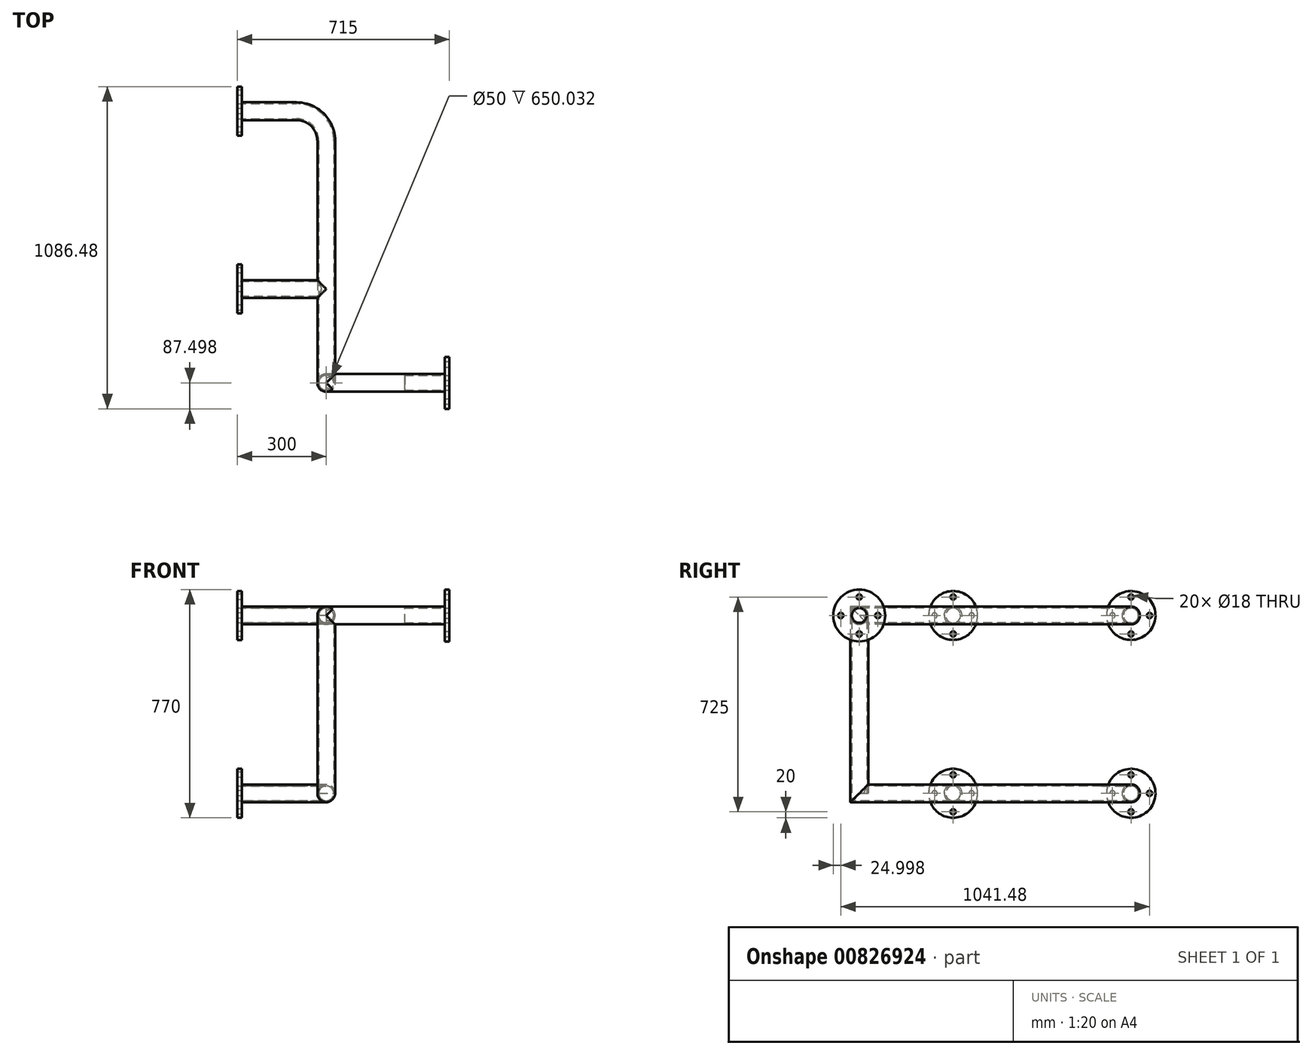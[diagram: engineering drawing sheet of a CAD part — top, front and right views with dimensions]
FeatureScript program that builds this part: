
annotation { "Feature Type Name" : "Feature", "Feature Type Description" : "" }
export const myFeature = defineFeature(function(context is Context, id is Id, definition is map)
    precondition{}
    {
        {
            var Q0;
            Q0=qCreatedBy(makeId("Top.planeOp"),FACE);
            var sketch = newSketch(context, id + "F0", { "sketchPlane" : qUnion([Q0])});
            skLineSegment(sketch, "E0.bottom", {"start": v(0, 0) * mm, "end": v(200, 0) * mm});
            skLineSegment(sketch, "E0.top", {"start": v(0, -600) * mm, "end": v(300, -600) * mm});
            skLineSegment(sketch, "E0.right", {"start": v(300, -100) * mm, "end": v(300, -600) * mm});
            skLineSegment(sketch, "E1", {"start": v(300, -600) * mm, "end": v(300, -916.48) * mm});
            skPoint(sketch, "E2.visualSharp", {"position": v(300, 0) * mm});
            skArc(sketch, "E2.filletArc", {"start": v(300, -100) * mm, "mid": v(270.71, -29.29) * mm, "end": v(200, 0) * mm});
            skSolve(sketch);
        }
        {
            var Q0;
            Q0=qCreatedBy(makeId("Top.planeOp"),FACE);
            cPlane(context, id + "F1", {"entities" : qUnion([Q0]), "cplaneType" : CPlaneType.OFFSET, "offset" : 600 * mm, "width" : 150 * mm, "height" : 150 * mm});
        }
        {
            var Q0;
            Q0=qCreatedBy(makeId("Right.planeOp"),FACE);
            cPlane(context, id + "F2", {"entities" : qUnion([Q0]), "cplaneType" : CPlaneType.OFFSET, "offset" : 300 * mm, "width" : 150 * mm, "height" : 150 * mm});
        }
        {
            var Q0;
            Q0=qCreatedBy(id+"F1.planeOp",FACE);
            var sketch = newSketch(context, id + "F3", { "sketchPlane" : qUnion([Q0])});
            skLineSegment(sketch, "E3.0", {"start": v(0, 0) * mm, "end": v(200, 0) * mm});
            skLineSegment(sketch, "E3.1", {"start": v(300, -100) * mm, "end": v(300, -600) * mm});
            skLineSegment(sketch, "E3.2", {"start": v(0, -600) * mm, "end": v(300, -600) * mm});
            skLineSegment(sketch, "E3.3", {"start": v(300, -600) * mm, "end": v(300, -916.48) * mm});
            skArc(sketch, "E3.4", {"start": v(300, -100) * mm, "mid": v(270.71, -29.29) * mm, "end": v(200, 0) * mm});
            skSolve(sketch);
        }
        {
            var Q0;
            Q0=qCreatedBy(makeId("Right.planeOp"),FACE);
            var sketch = newSketch(context, id + "F4", { "sketchPlane" : qUnion([Q0])});
            skCircle(sketch, "E4", {"center": v(0, 0) * mm, "radius": 25 * mm});
            skCircle(sketch, "E5", {"center": v(0, 0) * mm, "radius": 30 * mm});
            skCircle(sketch, "E6.0.1.0", {"center": v(0, 600) * mm, "radius": 30 * mm});
            skCircle(sketch, "E6.0.1.1", {"center": v(0, 600) * mm, "radius": 25 * mm});
            skCircle(sketch, "E6.1.0.0", {"center": v(-600, 0) * mm, "radius": 30 * mm});
            skCircle(sketch, "E6.1.0.1", {"center": v(-600, 0) * mm, "radius": 25 * mm});
            skCircle(sketch, "E6.1.1.0", {"center": v(-600, 600) * mm, "radius": 30 * mm});
            skCircle(sketch, "E6.1.1.1", {"center": v(-600, 600) * mm, "radius": 25 * mm});
            skLineSegment(sketch, "E6.direction1", {"start": v(0, 0) * mm, "end": v(-600, 0) * mm, "construction": true});
            skLineSegment(sketch, "E6.direction2", {"start": v(0, 0) * mm, "end": v(0, 600) * mm, "construction": true});
            skSolve(sketch);
        }
        {
            var Q0;
            Q0=makeQuery(id+"F4.imprint","IMPRINT",FACE,{"disambiguationData":[TD([[makeQuery(id+"F4.imprint","IMPRINT",EDGE,{"derivedFrom":sQuery(id+"F4.wireOp",EDGE,"E6.0.1.0")}),1.0]])]});
            var sketch = newSketch(context, id + "F5", { "sketchPlane" : qUnion([Q0])});
            skPoint(sketch, "E7.0", {"position": v(0, 600) * mm});
            skCircle(sketch, "E8", {"center": v(0, 600) * mm, "radius": 82.5 * mm});
            skCircle(sketch, "E9", {"center": v(0, 662.5) * mm, "radius": 9 * mm});
            skCircle(sketch, "E10.1.0", {"center": v(-62.5, 600) * mm, "radius": 9 * mm});
            skCircle(sketch, "E10.2.0", {"center": v(0, 537.5) * mm, "radius": 9 * mm});
            skCircle(sketch, "E10.3.0", {"center": v(62.5, 600) * mm, "radius": 9 * mm});
            skCircle(sketch, "E11.0.0", {"center": v(0, 600) * mm, "radius": 25 * mm});
            skCircle(sketch, "E12.0.1.0", {"center": v(0, -62.5) * mm, "radius": 9 * mm});
            skCircle(sketch, "E12.0.1.1", {"center": v(-62.5, 0) * mm, "radius": 9 * mm});
            skCircle(sketch, "E12.0.1.2", {"center": v(0, 0) * mm, "radius": 82.5 * mm});
            skCircle(sketch, "E12.0.1.3", {"center": v(62.5, 0) * mm, "radius": 9 * mm});
            skPoint(sketch, "E12.0.1.4", {"position": v(0, 0) * mm});
            skCircle(sketch, "E12.0.1.5", {"center": v(0, 62.5) * mm, "radius": 9 * mm});
            skCircle(sketch, "E12.0.1.6", {"center": v(0, 0) * mm, "radius": 25 * mm});
            skPoint(sketch, "E12.0.1.7", {"position": v(0, 0) * mm});
            skCircle(sketch, "E12.1.0.0", {"center": v(-600, 537.5) * mm, "radius": 9 * mm});
            skCircle(sketch, "E12.1.0.1", {"center": v(-662.5, 600) * mm, "radius": 9 * mm});
            skCircle(sketch, "E12.1.0.2", {"center": v(-600, 600) * mm, "radius": 82.5 * mm});
            skCircle(sketch, "E12.1.0.3", {"center": v(-537.5, 600) * mm, "radius": 9 * mm});
            skPoint(sketch, "E12.1.0.4", {"position": v(-600, 600) * mm});
            skCircle(sketch, "E12.1.0.5", {"center": v(-600, 662.5) * mm, "radius": 9 * mm});
            skCircle(sketch, "E12.1.0.6", {"center": v(-600, 600) * mm, "radius": 25 * mm});
            skPoint(sketch, "E12.1.0.7", {"position": v(-600, 600) * mm});
            skCircle(sketch, "E12.1.1.0", {"center": v(-600, -62.5) * mm, "radius": 9 * mm});
            skCircle(sketch, "E12.1.1.1", {"center": v(-662.5, 0) * mm, "radius": 9 * mm});
            skCircle(sketch, "E12.1.1.2", {"center": v(-600, 0) * mm, "radius": 82.5 * mm});
            skCircle(sketch, "E12.1.1.3", {"center": v(-537.5, 0) * mm, "radius": 9 * mm});
            skPoint(sketch, "E12.1.1.4", {"position": v(-600, 0) * mm});
            skCircle(sketch, "E12.1.1.5", {"center": v(-600, 62.5) * mm, "radius": 9 * mm});
            skCircle(sketch, "E12.1.1.6", {"center": v(-600, 0) * mm, "radius": 25 * mm});
            skPoint(sketch, "E12.1.1.7", {"position": v(-600, 0) * mm});
            skLineSegment(sketch, "E12.direction1", {"start": v(0, 537.5) * mm, "end": v(-600, 537.5) * mm, "construction": true});
            skLineSegment(sketch, "E12.direction2", {"start": v(0, 537.5) * mm, "end": v(0, -62.5) * mm, "construction": true});
            skSolve(sketch);
        }
        {
            var Q0;
            Q0=qCreatedBy(id+"F2.planeOp",FACE);
            var sketch = newSketch(context, id + "F6", { "sketchPlane" : qUnion([Q0])});
            skLineSegment(sketch, "E13.0", {"start": v(-600, 600) * mm, "end": v(-916.48, 600) * mm});
            skLineSegment(sketch, "E14.0", {"start": v(-600, 0) * mm, "end": v(-916.48, 0) * mm});
            skLineSegment(sketch, "E15", {"start": v(-916.48, 600) * mm, "end": v(-916.48, 0) * mm});
            skSolve(sketch);
        }
        {
            var Q0;
            Q0=makeQuery(id+"F4.imprint","IMPRINT",FACE,{"disambiguationData":[TD([[makeQuery(id+"F4.imprint","IMPRINT",EDGE,{"derivedFrom":sQuery(id+"F4.wireOp",EDGE,"E6.0.1.0")}),1.0]])]});
            var Q1;
            Q1=sQuery(id+"F3.wireOp",EDGE,"E3.0");
            var Q2;
            Q2=sQuery(id+"F3.wireOp",EDGE,"E3.4");
            var Q3;
            Q3=sQuery(id+"F3.wireOp",EDGE,"E3.1");
            var Q4;
            Q4=sQuery(id+"F3.wireOp",EDGE,"E3.3");
            var Q5;
            Q5=sQuery(id+"F6.wireOp",EDGE,"E15");
            sweep(context, id + "F7", {"profiles" : qUnion([Q0]), "path" : qUnion([Q1, Q2, Q3, Q4, Q5])});
        }
        {
            var Q0;
            Q0=makeQuery(id+"F4.imprint","IMPRINT",FACE,{"disambiguationData":[TD([[makeQuery(id+"F4.imprint","IMPRINT",EDGE,{"derivedFrom":sQuery(id+"F4.wireOp",EDGE,"E4")}),-1.0]])]});
            var Q1;
            Q1=sQuery(id+"F0.wireOp",EDGE,"E0.bottom");
            var Q2;
            Q2=sQuery(id+"F0.wireOp",EDGE,"E2.filletArc");
            var Q3;
            Q3=sQuery(id+"F0.wireOp",EDGE,"E0.right");
            var Q4;
            Q4=sQuery(id+"F0.wireOp",EDGE,"E1");
            var Q5;
            Q5=sQuery(id+"F6.wireOp",EDGE,"E15");
            sweep(context, id + "F8", {"operationType" : NewBodyOperationType.ADD, "profiles" : qUnion([Q0]), "path" : qUnion([Q1, Q2, Q3, Q4, Q5])});
        }
        {
            var Q0;
            Q0=makeQuery(id+"F4.imprint","IMPRINT",FACE,{"disambiguationData":[TD([[makeQuery(id+"F4.imprint","IMPRINT",EDGE,{"derivedFrom":sQuery(id+"F4.wireOp",EDGE,"E6.1.1.0")}),1.0]])]});
            extrude(context, id + "F9", {"entities" : qUnion([Q0]), "operationType" : NewBodyOperationType.ADD, "endBound" : BoundingType.UP_TO_NEXT, "depth" : 25 * mm, "offsetDistance" : 25 * mm});
        }
        {
            var Q0;
            Q0=makeQuery(id+"F4.imprint","IMPRINT",FACE,{"disambiguationData":[TD([[makeQuery(id+"F4.imprint","IMPRINT",EDGE,{"derivedFrom":sQuery(id+"F4.wireOp",EDGE,"E6.1.0.0")}),1.0]])]});
            extrude(context, id + "F10", {"entities" : qUnion([Q0]), "operationType" : NewBodyOperationType.ADD, "endBound" : BoundingType.UP_TO_NEXT, "depth" : 25 * mm, "offsetDistance" : 25 * mm});
        }
        {
            var Q0;
            Q0 = qSketchRegion(id + "F5", true);
            extrude(context, id + "F11", {"entities" : qUnion([Q0]), "operationType" : NewBodyOperationType.ADD, "depth" : 15 * mm, "offsetDistance" : 25 * mm});
        }
        {
            var Q0;
            Q0=qCreatedBy(makeId("Front.planeOp"),FACE);
            cPlane(context, id + "F12", {"entities" : qUnion([Q0]), "cplaneType" : CPlaneType.OFFSET, "offset" : (920 - 3.52) * mm, "width" : 150 * mm, "height" : 150 * mm});
        }
        {
            var Q0;
            Q0=qCreatedBy(id+"F12.planeOp",FACE);
            var sketch = newSketch(context, id + "F13", { "sketchPlane" : qUnion([Q0])});
            skPoint(sketch, "E16.0", {"position": v(300, 600) * mm});
            skLineSegment(sketch, "E17", {"start": v(300, 600) * mm, "end": v(500, 600) * mm});
            skSolve(sketch);
        }
        {
            var Q0;
            Q0=qCreatedBy(id+"F2.planeOp",FACE);
            var sketch = newSketch(context, id + "F14", { "sketchPlane" : qUnion([Q0])});
            skPoint(sketch, "E18.0", {"position": v(-916.48, 600) * mm});
            skCircle(sketch, "E19", {"center": v(-916.48, 600) * mm, "radius": 30 * mm});
            skSolve(sketch);
        }
        {
            var Q0;
            Q0 = qSketchRegion(id + "F14", true);
            extrude(context, id + "F15", {"entities" : qUnion([Q0]), "operationType" : NewBodyOperationType.ADD, "depth" : 415 * mm, "offsetDistance" : 25 * mm});
        }
        {
            var Q0;
            Q0=makeQuery(id+"F15.opExtrude","CAP_FACE",FACE,{"disambiguationData":[OSD([sQuery(id+"F14.wireOp",EDGE,"E19")])],"isStart":false});
            var sketch = newSketch(context, id + "F16", { "sketchPlane" : qUnion([Q0])});
            skCircle(sketch, "E20", {"center": v(-916.48, 600) * mm, "radius": 87.5 * mm});
            skCircle(sketch, "E21", {"center": v(-916.48, 537.5) * mm, "radius": 9 * mm});
            skCircle(sketch, "E22", {"center": v(-916.48, 600) * mm, "radius": 25 * mm});
            skCircle(sketch, "E23.1.0", {"center": v(-853.98, 600) * mm, "radius": 9 * mm});
            skCircle(sketch, "E23.2.0", {"center": v(-916.48, 662.5) * mm, "radius": 9 * mm});
            skCircle(sketch, "E23.3.0", {"center": v(-978.98, 600) * mm, "radius": 9 * mm});
            skCircle(sketch, "E24.0", {"center": v(-916.48, 600) * mm, "radius": 30 * mm});
            skSolve(sketch);
        }
        {
            var Q0;
            Q0=makeQuery(id+"F16.imprint","IMPRINT",FACE,{"disambiguationData":[TD([[makeQuery(id+"F16.imprint","IMPRINT",EDGE,{"derivedFrom":sQuery(id+"F16.wireOp",EDGE,"E20")}),1.0]])]});
            extrude(context, id + "F17", {"entities" : qUnion([Q0]), "operationType" : NewBodyOperationType.ADD, "oppositeDirection" : true, "depth" : 15 * mm, "offsetDistance" : 25 * mm});
        }
        {
            var Q0;
            Q0=makeQuery(id+"F16.imprint","IMPRINT",FACE,{"disambiguationData":[TD([[makeQuery(id+"F16.imprint","IMPRINT",EDGE,{"derivedFrom":sQuery(id+"F16.wireOp",EDGE,"E22")}),1.0]])]});
            extrude(context, id + "F18", {"entities" : qUnion([Q0]), "operationType" : NewBodyOperationType.REMOVE, "oppositeDirection" : true, "depth" : 150 * mm, "offsetDistance" : 25 * mm});
        }
    });
